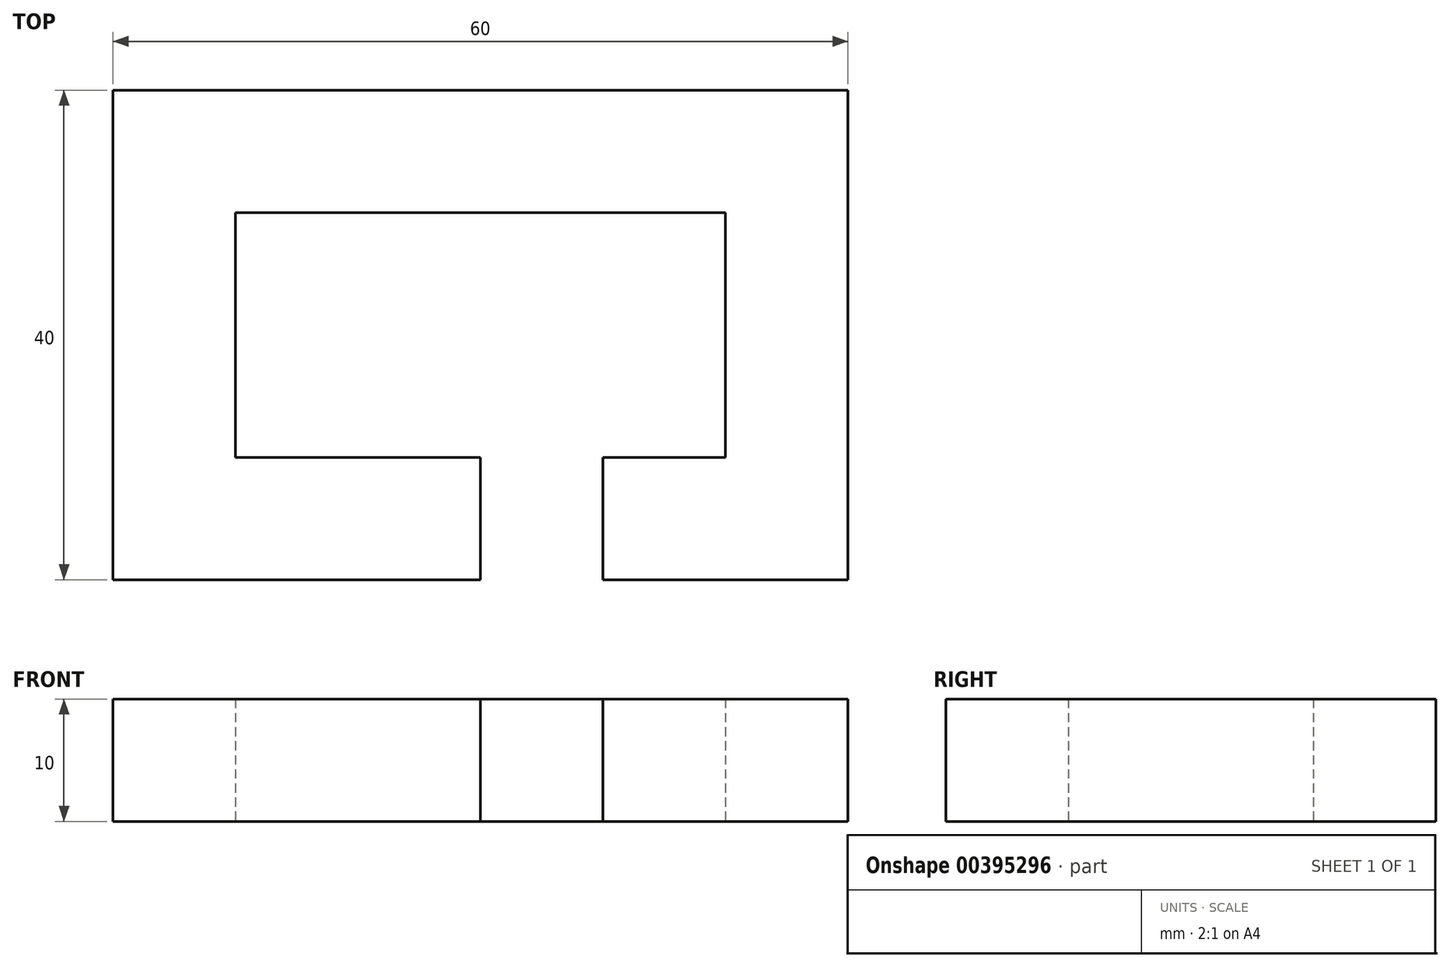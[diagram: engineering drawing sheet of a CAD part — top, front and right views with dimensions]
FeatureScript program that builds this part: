
annotation { "Feature Type Name" : "Feature", "Feature Type Description" : "" }
export const myFeature = defineFeature(function(context is Context, id is Id, definition is map)
    precondition{}
    {
        {
            var Q0;
            Q0=qCreatedBy(makeId("Top.planeOp"),FACE);
            var sketch = newSketch(context, id + "F0", { "sketchPlane" : qUnion([Q0])});
            skLineSegment(sketch, "E0.bottom", {"start": v(-30, 20) * mm, "end": v(30, 20) * mm});
            skLineSegment(sketch, "E0.top", {"start": v(-30, -20) * mm, "end": v(30, -20) * mm});
            skLineSegment(sketch, "E0.left", {"start": v(-30, 20) * mm, "end": v(-30, -20) * mm});
            skLineSegment(sketch, "E0.right", {"start": v(30, 20) * mm, "end": v(30, -20) * mm});
            skPoint(sketch, "E0.middle", {"position": v(0, 0) * mm});
            skLineSegment(sketch, "E1.bottom", {"start": v(-20, 10) * mm, "end": v(20, 10) * mm});
            skLineSegment(sketch, "E1.top", {"start": v(-20, -10) * mm, "end": v(20, -10) * mm});
            skLineSegment(sketch, "E1.left", {"start": v(-20, 10) * mm, "end": v(-20, -10) * mm});
            skLineSegment(sketch, "E1.right", {"start": v(20, 10) * mm, "end": v(20, -10) * mm});
            skLineSegment(sketch, "E2", {"start": v(20, -10) * mm, "end": v(10, -10) * mm, "construction": true});
            skLineSegment(sketch, "E3", {"start": v(10, -10) * mm, "end": v(10, -20) * mm});
            skLineSegment(sketch, "E4", {"start": v(10, -10) * mm, "end": v(0, -10) * mm, "construction": true});
            skLineSegment(sketch, "E5", {"start": v(0, -10) * mm, "end": v(0, -20) * mm});
            skSolve(sketch);
        }
        {
            var Q0;
            Q0=makeQuery(id+"F0.imprint","IMPRINT",FACE,{"disambiguationData":[TD([[makeQuery(id+"F0.imprint","IMPRINT",EDGE,{"derivedFrom":sQuery(id+"F0.wireOp",EDGE,"E0.bottom")}),-1.0]])]});
            extrude(context, id + "F1", {"entities" : qUnion([Q0]), "depth" : 10 * mm});
        }
    });
